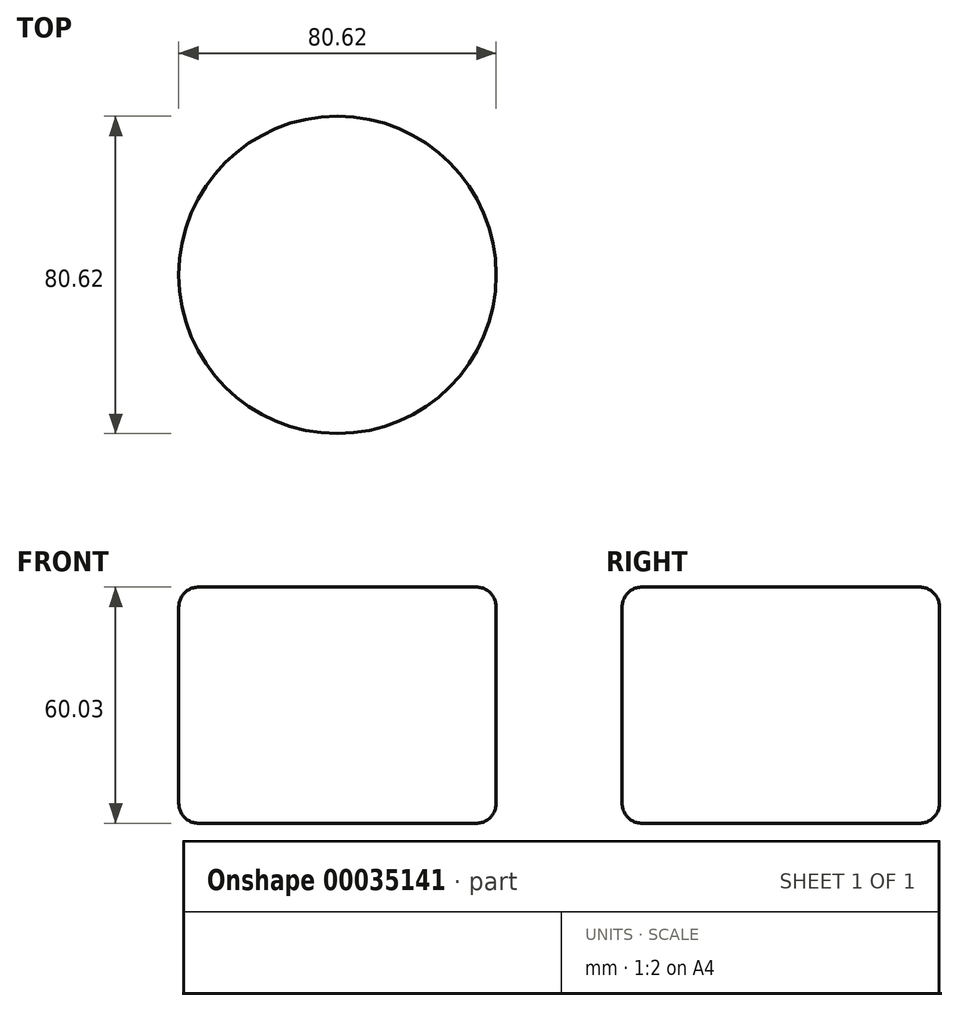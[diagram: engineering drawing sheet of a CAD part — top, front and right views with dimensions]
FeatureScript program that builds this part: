
annotation { "Feature Type Name" : "Feature", "Feature Type Description" : "" }
export const myFeature = defineFeature(function(context is Context, id is Id, definition is map)
    precondition{}
    {
        {
            var Q0;
            Q0=qCreatedBy(makeId("Top.planeOp"),FACE);
            var sketch = newSketch(context, id + "F0", { "sketchPlane" : qUnion([Q0])});
            skCircle(sketch, "E0", {"center": v(0, 0) * mm, "radius": 40.31 * mm});
            skSolve(sketch);
        }
        {
            var Q0;
            Q0=makeQuery(id+"F0.imprint","IMPRINT",FACE,{"disambiguationData":[TD([[makeQuery(id+"F0.imprint","IMPRINT",EDGE,{"derivedFrom":sQuery(id+"F0.wireOp",EDGE,"E0")}),1.0]])]});
            extrude(context, id + "F1", {"entities" : qUnion([Q0]), "depth" : 60.03 * mm});
        }
        {
            var Q0;
            Q0=makeQuery(id+"F1.opExtrude","CAP_EDGE",EDGE,{"disambiguationData":[OSD([sQuery(id+"F0.wireOp",EDGE,"E0")])],"isStart":false});
            var Q1;
            Q1=makeQuery(id+"F1.opExtrude","CAP_EDGE",EDGE,{"disambiguationData":[OSD([sQuery(id+"F0.wireOp",EDGE,"E0")])],"isStart":true});
            fillet(context, id + "F2", {"entities" : qUnion([Q0, Q1]), "radius" : 5.08 * mm, "tangentPropagation" : true, "allowEdgeOverflow" : false});
        }
    });
